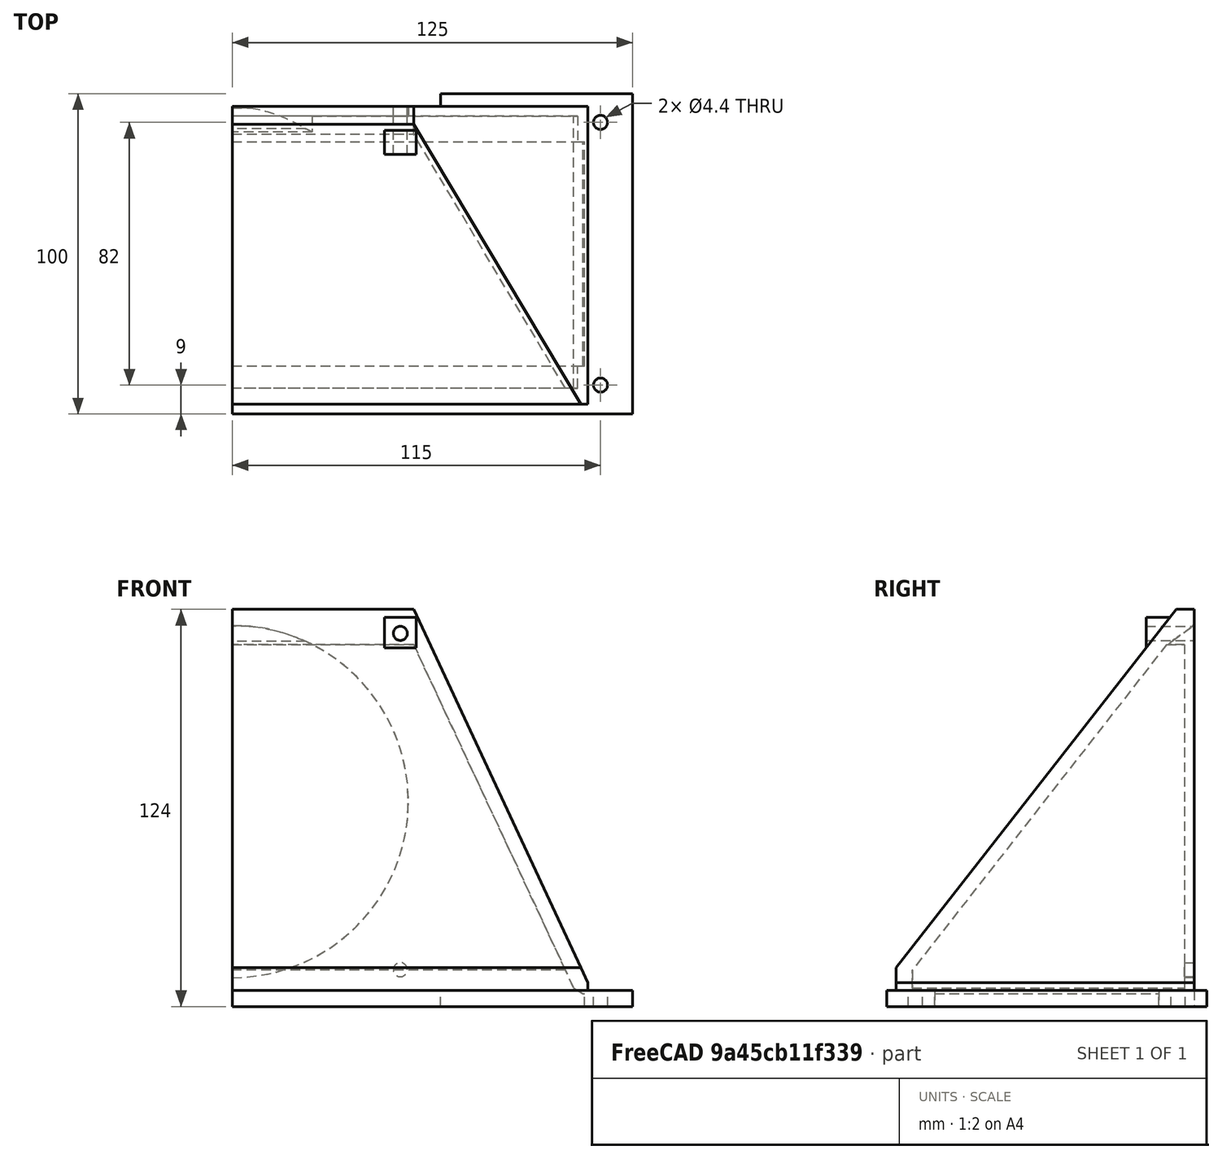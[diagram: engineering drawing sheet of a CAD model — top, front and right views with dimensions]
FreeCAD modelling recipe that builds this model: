
FCSTD DOCUMENT  (FreeCAD 0.16R6703 (Git))
Label: freezer-fan
License: All rights reserved
LicenseURL: http://en.wikipedia.org/wiki/All_rights_reserved
objects: Part::Box×16, Part::Cut×12, Part::Cylinder×9, Part::MultiFuse×7, Part::Chamfer×6, Part::Mirroring×4
note: 54 computed .brp shape members not serialized (recipe doc carries the construction recipe); baked Part::Feature solids carry a one-line shape summary decoded from their .brp

FEATURE [Part::Cylinder] Cylinder
  Angle = 360
  Height = 50
  Placement = pos=(-115,-41,0) rot=(0,0,1;0rad)
  Radius = 2.2
FEATURE [Part::Cylinder] Cylinder001
  Angle = 360
  Height = 50
  Placement = pos=(115,-41,0) rot=(0,0,1;0rad)
  Radius = 2.2
FEATURE [Part::Cylinder] Cylinder002
  Angle = 360
  Height = 50
  Placement = pos=(-115,41,0) rot=(0,0,1;0rad)
  Radius = 2.2
FEATURE [Part::Cylinder] Cylinder003
  Angle = 360
  Height = 50
  Placement = pos=(115,41,0) rot=(0,0,1;0rad)
  Radius = 2.2
FEATURE [Part::Cylinder] Cylinder004
  Angle = 360
  Height = 50
  Placement = pos=(-52.5,-52.5,0) rot=(0,0,1;0rad)
  Radius = 2.2
FEATURE [Part::Cylinder] Cylinder005
  Angle = 360
  Height = 50
  Placement = pos=(52.5,52.5,0) rot=(0,0,1;0rad)
  Radius = 2.2
FEATURE [Part::Cylinder] Cylinder006
  Angle = 360
  Height = 50
  Placement = pos=(-52.5,52.5,0) rot=(0,0,1;0rad)
  Radius = 2.2
FEATURE [Part::Cylinder] Cylinder007
  Angle = 360
  Height = 50
  Placement = pos=(52.5,-52.5,0) rot=(0,0,1;0rad)
  Radius = 2.2
FEATURE [Part::MultiFuse] Fusion  label="fan-holes"
  Placement = pos=(0,15,64) rot=(-1,0,0;1.5708rad)
  Shapes = -> [Cylinder004,Cylinder007,Cylinder005,Cylinder006]
FEATURE [Part::MultiFuse] Fusion001  label="mount-holes"
  Placement = pos=(0,0,-1) rot=(0,0,1;0rad)
  Shapes = -> [Cylinder,Cylinder002,Cylinder003,Cylinder001]
FEATURE [Part::Box] Box  label="Cube"
  Height = 5
  Length = 250
  Placement = pos=(-125,-50,0) rot=(0,0,1;0rad)
  Width = 100
FEATURE [Part::Box] Box001  label="Cube001"
  Height = 12
  Length = 220
  Placement = pos=(-110,-35,-1) rot=(0,0,1;0rad)
  Width = 70
FEATURE [Part::Cut] Cut
  Base = -> Box
  Tool = -> Box001
FEATURE [Part::Cut] Cut001
  Base = -> Cut
  Tool = -> Fusion001
FEATURE [Part::Box] Box002  label="Cube002"
  Height = 200
  Length = 120
  Placement = pos=(-245,-55,4) rot=(0,1,0;0.436332rad)
  Width = 104
FEATURE [Part::Cylinder] Cylinder008
  Angle = 360
  Height = 10
  Placement = pos=(0,49,64) rot=(1,0,0;1.5708rad)
  Radius = 55
FEATURE [Part::Box] Box003  label="Cube003"
  Height = 120
  Length = 222
  Placement = pos=(-111,-47,4) rot=(0,0,1;0rad)
  Width = 93
FEATURE [Part::Box] Box004  label="Cube004"
  Height = 249
  Length = 234
  Placement = pos=(-121,-144,39) rot=(-1,0,0;0.663225rad)
  Width = 93
FEATURE [Part::Box] Box005  label="Cube005"
  Height = 200
  Length = 120
  Placement = pos=(-245,-55,4) rot=(0,1,0;0.436332rad)
  Width = 104
FEATURE [Part::Mirroring] Part__Mirroring  label="Cube005 (Mirror #1)"
  Base = (0,0,0)
  Normal = (1,0,0)
  Source = -> Box005
FEATURE [Part::MultiFuse] Fusion002
  Shapes = -> [Box002,Part__Mirroring]
FEATURE [Part::Cut] Cut002
  Base = -> Box003
  Tool = -> Fusion002
FEATURE [Part::Cut] Cut003
  Base = -> Cut002
  Tool = -> Box004
FEATURE [Part::Box] Box006  label="Cube006"
  Height = 200
  Length = 120
  Placement = pos=(-245,-55,4) rot=(0,1,0;0.436332rad)
  Width = 104
FEATURE [Part::Box] Box007  label="Cube007"
  Height = 120
  Length = 222
  Placement = pos=(-111,-47,4) rot=(0,0,1;0rad)
  Width = 93
FEATURE [Part::Box] Box008  label="Cube008"
  Height = 249
  Length = 234
  Placement = pos=(-121,-144,39) rot=(-1,0,0;0.663225rad)
  Width = 93
FEATURE [Part::Box] Box009  label="Cube009"
  Height = 200
  Length = 120
  Placement = pos=(-245,-55,4) rot=(0,1,0;0.436332rad)
  Width = 104
FEATURE [Part::Mirroring] Part__Mirroring001  label="Cube005 (Mirror #1)001"
  Base = (0,0,0)
  Normal = (1,0,0)
  Source = -> Box009
FEATURE [Part::MultiFuse] Fusion003
  Shapes = -> [Box006,Part__Mirroring001]
FEATURE [Part::Cut] Cut004
  Base = -> Box007
  Tool = -> Fusion003
FEATURE [Part::Cut] Cut005
  Base = -> Cut004
  Placement = pos=(0,-3,-11) rot=(0,0,1;0rad)
  Tool = -> Box008
FEATURE [Part::Box] Box010  label="Cube010"
  Height = 41
  Length = 300
  Placement = pos=(-150,-62,-12) rot=(0,0,1;0rad)
  Width = 20
FEATURE [Part::Cut] Cut006
  Base = -> Cut005
  Tool = -> Box010
FEATURE [Part::Cut] Cut007
  Base = -> Cut003
  Tool = -> Cut006
FEATURE [Part::Cut] Cut008
  Base = -> Cut007
  Tool = -> Cylinder008
FEATURE [Part::MultiFuse] Fusion004
  Shapes = -> [Cut008,Cut001]
FEATURE [Part::Box] Box011  label="Cube011"
  Height = 10
  Length = 130
  Placement = pos=(-65,46,-2) rot=(0,0,1;0rad)
  Width = 10
FEATURE [Part::Cut] Cut009
  Base = -> Fusion004
  Tool = -> Box011
FEATURE [Part::Chamfer] Chamfer
  Base = -> Cut009
  Edges = 1 edges r=2: [Edge88]
FEATURE [Part::Chamfer] Chamfer001
  Base = -> Chamfer
  Edges = 1 edges r=2: [Edge21]
FEATURE [Part::Box] Box012  label="Cube012"
  Height = 10
  Length = 10
  Placement = pos=(47.5,31,111.5) rot=(0,0,1;0rad)
  Width = 8
FEATURE [Part::Chamfer] Chamfer002
  Base = -> Box012
  Edges = 1 edges r=6: [Edge11]
FEATURE [Part::Box] Box013  label="Cube013"
  Height = 10
  Length = 10
  Placement = pos=(47.5,31,111.5) rot=(0,0,1;0rad)
  Width = 8
FEATURE [Part::Chamfer] Chamfer003
  Base = -> Box013
  Edges = 1 edges r=6: [Edge11]
FEATURE [Part::Mirroring] Part__Mirroring002  label="Chamfer003 (Mirror #3)"
  Base = (0,0,0)
  Normal = (1,0,0)
  Source = -> Chamfer003
FEATURE [Part::MultiFuse] Fusion005
  Shapes = -> [Chamfer001,Part__Mirroring002,Chamfer002]
FEATURE [Part::Cut] Cut010
  Base = -> Fusion005
  Tool = -> Fusion
FEATURE [Part::Chamfer] Chamfer004
  Base = -> Cut010
  Edges = 1 edges r=1: [Edge34]
FEATURE [Part::Box] Box014  label="Cube014"
  Height = 150
  Length = 150
  Placement = pos=(0,-70,-1) rot=(0,0,1;0rad)
  Width = 150
FEATURE [Part::Cut] Cut011
  Base = -> Chamfer004
  Tool = -> Box014
FEATURE [Part::Box] Box015  label="Cube015"
  Height = 5
  Length = 30
  Placement = pos=(-30,39,114) rot=(1,0,0;0.628319rad)
  Width = 9
FEATURE [Part::Chamfer] Chamfer005
  Base = -> Box015
  Edges = 1 edges r=1: [Edge11]
FEATURE [Part::MultiFuse] Fusion006
  Shapes = -> [Cut011,Chamfer005]
FEATURE [Part::Mirroring] Part__Mirroring003  label="Fusion006 (Mirror #4)"
  Base = (0,0,0)
  Normal = (1,0,0)
  Source = -> Fusion006
